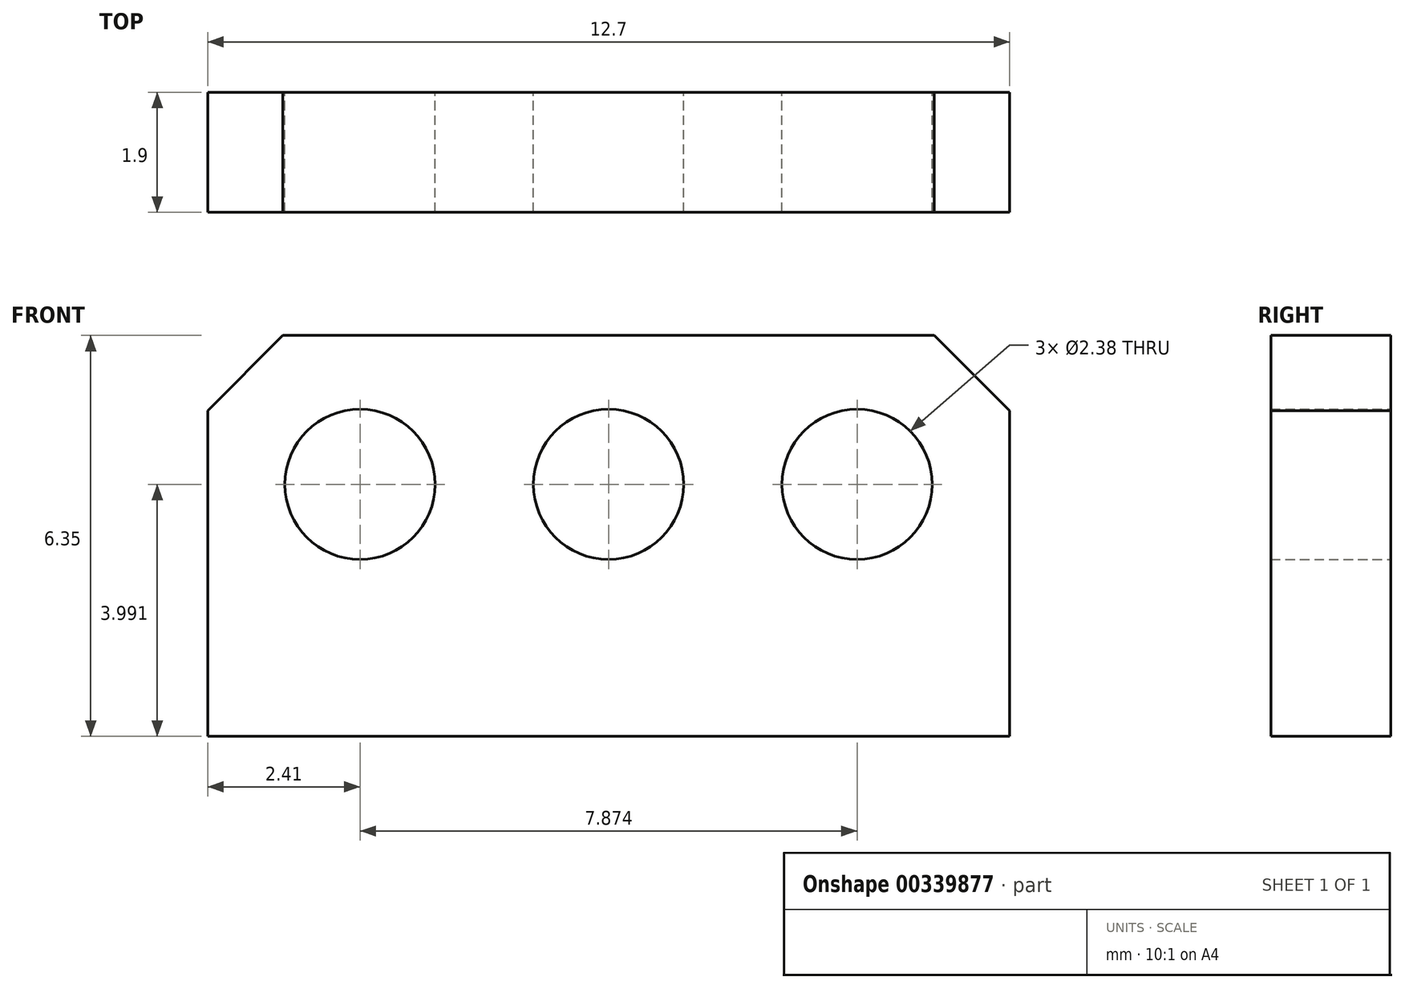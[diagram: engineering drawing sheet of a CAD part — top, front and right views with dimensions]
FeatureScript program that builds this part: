
annotation { "Feature Type Name" : "Feature", "Feature Type Description" : "" }
export const myFeature = defineFeature(function(context is Context, id is Id, definition is map)
    precondition{}
    {
        {
            var Q0;
            Q0=qCreatedBy(makeId("Front.planeOp"),FACE);
            var sketch = newSketch(context, id + "F0", { "sketchPlane" : qUnion([Q0])});
            skLineSegment(sketch, "E0.bottom", {"start": v(-50.52, 11.97) * mm, "end": v(-40.2, 11.97) * mm});
            skLineSegment(sketch, "E0.top", {"start": v(-51.71, 5.62) * mm, "end": v(-39.01, 5.62) * mm});
            skLineSegment(sketch, "E0.left", {"start": v(-51.71, 10.78) * mm, "end": v(-51.71, 5.62) * mm});
            skLineSegment(sketch, "E0.right", {"start": v(-39.01, 10.78) * mm, "end": v(-39.01, 5.62) * mm});
            skCircle(sketch, "E1", {"center": v(-49.3, 9.61) * mm, "radius": 1.19 * mm});
            skCircle(sketch, "E2.MirrorC", {"center": v(-41.43, 9.61) * mm, "radius": 1.19 * mm});
            skCircle(sketch, "E3", {"center": v(-45.36, 9.61) * mm, "radius": 1.19 * mm});
            skLineSegment(sketch, "E4", {"start": v(-51.71, 10.78) * mm, "end": v(-50.52, 11.97) * mm});
            skLineSegment(sketch, "E5", {"start": v(-40.2, 11.97) * mm, "end": v(-39.01, 10.78) * mm});
            skSolve(sketch);
        }
        {
            var Q0;
            Q0=makeQuery(id+"F0.imprint","IMPRINT",FACE,{"disambiguationData":[TD([[makeQuery(id+"F0.imprint","IMPRINT",EDGE,{"derivedFrom":sQuery(id+"F0.wireOp",EDGE,"E0.bottom")}),-1.0]])]});
            extrude(context, id + "F1", {"entities" : qUnion([Q0]), "depth" : 1.9 * mm});
        }
    });
